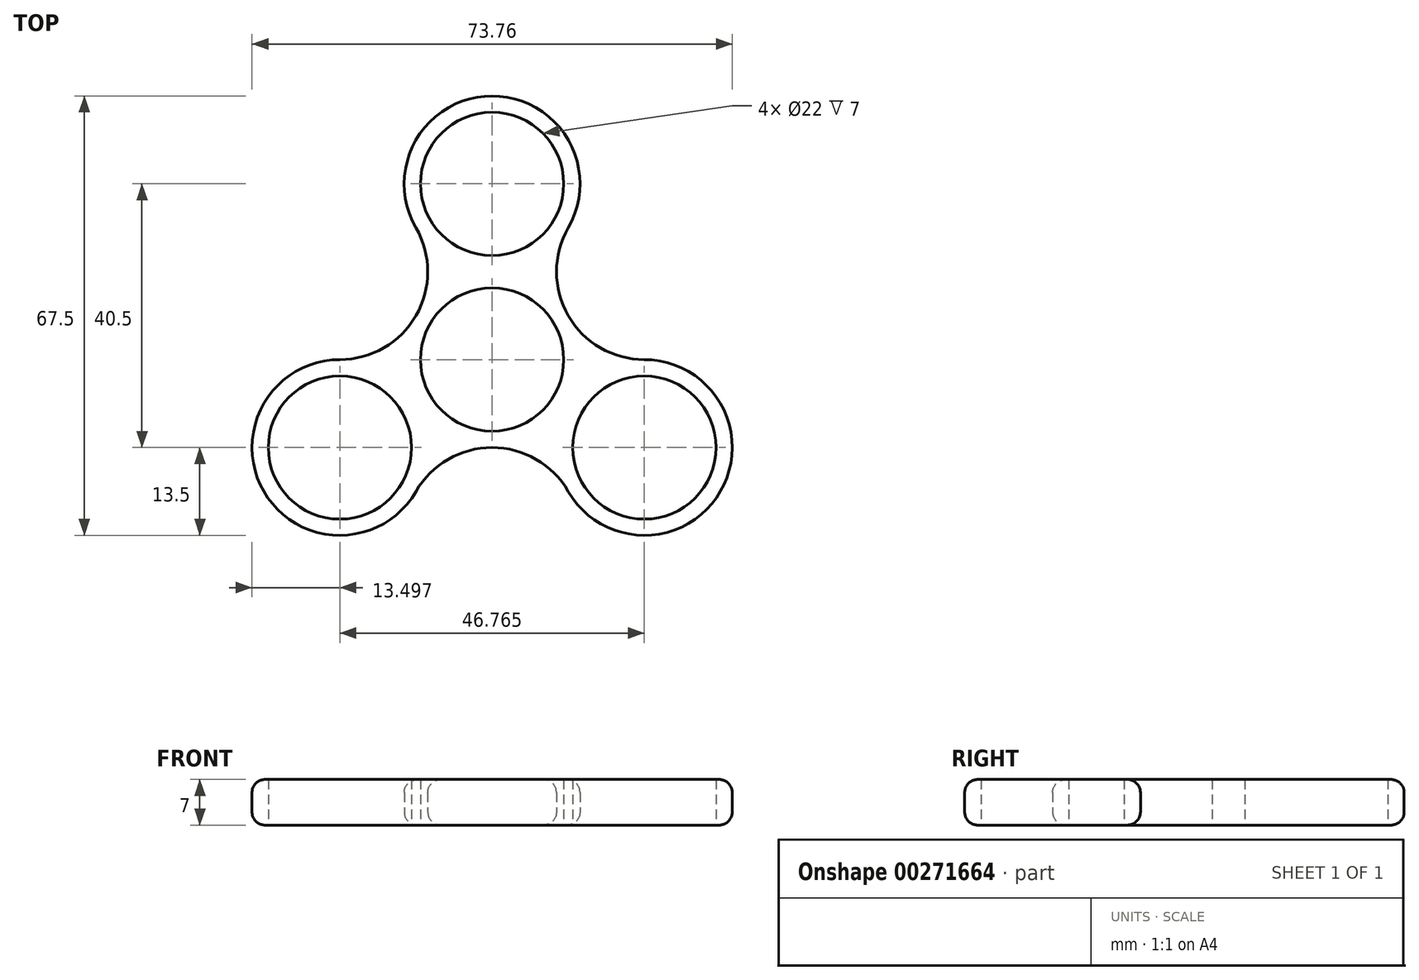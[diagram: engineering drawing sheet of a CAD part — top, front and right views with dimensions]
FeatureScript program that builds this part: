
annotation { "Feature Type Name" : "Feature", "Feature Type Description" : "" }
export const myFeature = defineFeature(function(context is Context, id is Id, definition is map)
    precondition{}
    {
        {
            var Q0;
            Q0=qCreatedBy(makeId("Top.planeOp"),FACE);
            var sketch = newSketch(context, id + "F0", { "sketchPlane" : qUnion([Q0])});
            skCircle(sketch, "E0", {"center": v(0, 0) * mm, "radius": 11 * mm});
            skCircle(sketch, "E1", {"center": v(0, 27) * mm, "radius": 11 * mm});
            skCircle(sketch, "E2", {"center": v(23.38, -13.5) * mm, "radius": 11 * mm});
            skCircle(sketch, "E3", {"center": v(-23.38, -13.5) * mm, "radius": 11 * mm});
            skLineSegment(sketch, "E4", {"start": v(0, 27) * mm, "end": v(-23.38, -13.5) * mm, "construction": true});
            skLineSegment(sketch, "E5", {"start": v(23.38, -13.5) * mm, "end": v(-23.38, -13.5) * mm, "construction": true});
            skLineSegment(sketch, "E6", {"start": v(23.38, -13.5) * mm, "end": v(0, 27) * mm, "construction": true});
            skLineSegment(sketch, "E7", {"start": v(-23.38, -13.5) * mm, "end": v(0, 0) * mm, "construction": true});
            skLineSegment(sketch, "E8", {"start": v(0, 0) * mm, "end": v(23.38, -13.5) * mm, "construction": true});
            skLineSegment(sketch, "E9", {"start": v(0, 0) * mm, "end": v(0, 27) * mm, "construction": true});
            skArc(sketch, "E10", {"start": v(11.7, 20.25) * mm, "mid": v(0, 40.5) * mm, "end": v(-11.7, 20.25) * mm});
            skArc(sketch, "E11", {"start": v(11.7, -20.25) * mm, "mid": v(35.07, -20.25) * mm, "end": v(23.38, 0) * mm});
            skArc(sketch, "E12", {"start": v(-23.38, 0) * mm, "mid": v(-35.07, -20.25) * mm, "end": v(-11.7, -20.25) * mm});
            skArc(sketch, "E13", {"start": v(11.7, 20.25) * mm, "mid": v(11.7, 6.75) * mm, "end": v(23.38, 0) * mm});
            skArc(sketch, "E14", {"start": v(-23.38, 0) * mm, "mid": v(-11.7, 6.75) * mm, "end": v(-11.7, 20.25) * mm});
            skArc(sketch, "E15", {"start": v(11.7, -20.25) * mm, "mid": v(0, -13.5) * mm, "end": v(-11.7, -20.25) * mm});
            skSolve(sketch);
        }
        {
            var Q0;
            Q0=makeQuery(id+"F0.imprint","IMPRINT",FACE,{"disambiguationData":[TD([[makeQuery(id+"F0.imprint","IMPRINT",EDGE,{"derivedFrom":sQuery(id+"F0.wireOp",EDGE,"E0")}),-1.0]])]});
            extrude(context, id + "F1", {"entities" : qUnion([Q0]), "depth" : 7 * mm});
        }
        {
            var Q0;
            Q0=makeQuery(id+"F1.opExtrude","CAP_EDGE",EDGE,{"disambiguationData":[OSD([sQuery(id+"F0.wireOp",EDGE,"E14")])],"isStart":false});
            var Q1;
            Q1=makeQuery(id+"F1.opExtrude","CAP_EDGE",EDGE,{"disambiguationData":[OSD([sQuery(id+"F0.wireOp",EDGE,"E13")])],"isStart":false});
            var Q2;
            Q2=makeQuery(id+"F1.opExtrude","CAP_EDGE",EDGE,{"disambiguationData":[OSD([sQuery(id+"F0.wireOp",EDGE,"E15")])],"isStart":false});
            fillet(context, id + "F2", {"entities" : qUnion([Q0, Q1, Q2]), "radius" : 2 * mm, "tangentPropagation" : true, "allowEdgeOverflow" : false});
        }
        {
            var Q0;
            Q0=makeQuery(id+"F1.opExtrude","CAP_EDGE",EDGE,{"disambiguationData":[OSD([sQuery(id+"F0.wireOp",EDGE,"E13")])],"isStart":true});
            fillet(context, id + "F3", {"entities" : qUnion([Q0]), "radius" : 2 * mm, "tangentPropagation" : true, "allowEdgeOverflow" : false});
        }
    });
